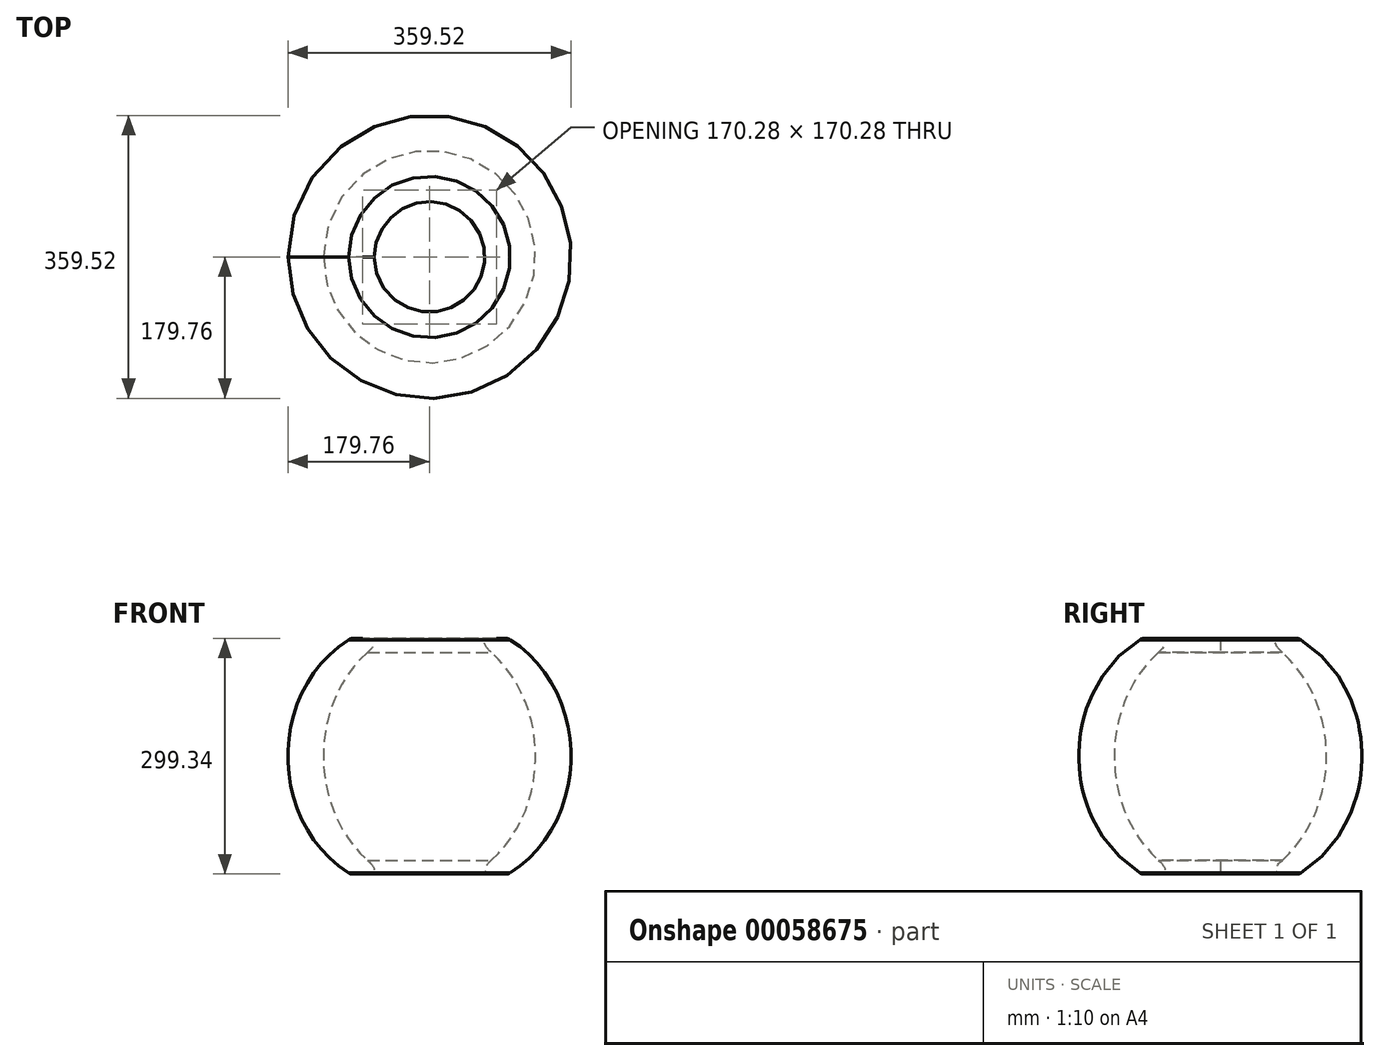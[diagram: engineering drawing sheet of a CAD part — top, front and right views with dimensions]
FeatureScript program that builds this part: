
annotation { "Feature Type Name" : "Feature", "Feature Type Description" : "" }
export const myFeature = defineFeature(function(context is Context, id is Id, definition is map)
    precondition{}
    {
        {
            var Q0;
            Q0=qCreatedBy(makeId("Front.planeOp"),FACE);
            var sketch = newSketch(context, id + "F0", { "sketchPlane" : qUnion([Q0])});
            skFitSpline(sketch, "E0", {"points": [v(-100, 149.67) * mm, v(-100, -149.67) * mm], "startDerivative": vector(-319.06, -194.46) * mm, "endDerivative": vector(319.06, -194.46) * mm});
            skFitSpline(sketch, "E1", {"points": [v(-55, 149.67) * mm, v(-55, -149.67) * mm], "startDerivative": vector(-319.06, -194.46) * mm, "endDerivative": vector(319.06, -194.46) * mm});
            skLineSegment(sketch, "E2", {"start": v(0, 0) * mm, "end": v(0, 123.33) * mm, "construction": true});
            skLineSegment(sketch, "E3", {"start": v(0, 123.33) * mm, "end": v(-15, 123.33) * mm, "construction": true});
            skLineSegment(sketch, "E4", {"start": v(-15, 123.33) * mm, "end": v(-15, 90.33) * mm, "construction": true});
            skLineSegment(sketch, "E5", {"start": v(-15, 90.33) * mm, "end": v(0, 90.33) * mm, "construction": true});
            skLineSegment(sketch, "E6", {"start": v(-25, 123.33) * mm, "end": v(-25, 90.33) * mm, "construction": true});
            skLineSegment(sketch, "E7", {"start": v(-100, 149.67) * mm, "end": v(-55, 149.67) * mm});
            skLineSegment(sketch, "E8", {"start": v(-100, -149.67) * mm, "end": v(-55, -149.67) * mm});
            skCircle(sketch, "E9", {"center": v(0, 0) * mm, "radius": 180 * mm, "construction": true});
            skLineSegment(sketch, "E10", {"start": v(0, 0) * mm, "end": v(-293.4, 0) * mm, "construction": true});
            skSolve(sketch);
        }
        {
            var Q0;
            Q0=makeQuery(id+"F0.imprint","IMPRINT",FACE,{"disambiguationData":[TD([[makeQuery(id+"F0.imprint","IMPRINT",EDGE,{"derivedFrom":sQuery(id+"F0.wireOp",EDGE,"E0")}),1.0]])]});
            var Q1;
            Q1=sQuery(id+"F0.wireOp",EDGE,"E2");
            revolve(context, id + "F1", {"entities" : qUnion([Q0]), "axis" : qUnion([Q1]), "revolveType" : RevolveType.FULL});
        }
        {
            var Q0;
            Q0=makeQuery(id+"F1.opRevolve","SWEPT_FACE",FACE,{"disambiguationData":[OSD([sQuery(id+"F0.wireOp",EDGE,"E8")])]});
            var Q1;
            Q1=makeQuery(id+"F1.opRevolve","SWEPT_FACE",FACE,{"disambiguationData":[OSD([sQuery(id+"F0.wireOp",EDGE,"E7")])]});
            fillet(context, id + "F2", {"entities" : qUnion([Q0, Q1]), "radius" : 10 * mm, "tangentPropagation" : true, "rho" : 0.5, "crossSection" : FilletCrossSection.CONIC, "allowEdgeOverflow" : false});
        }
    });
